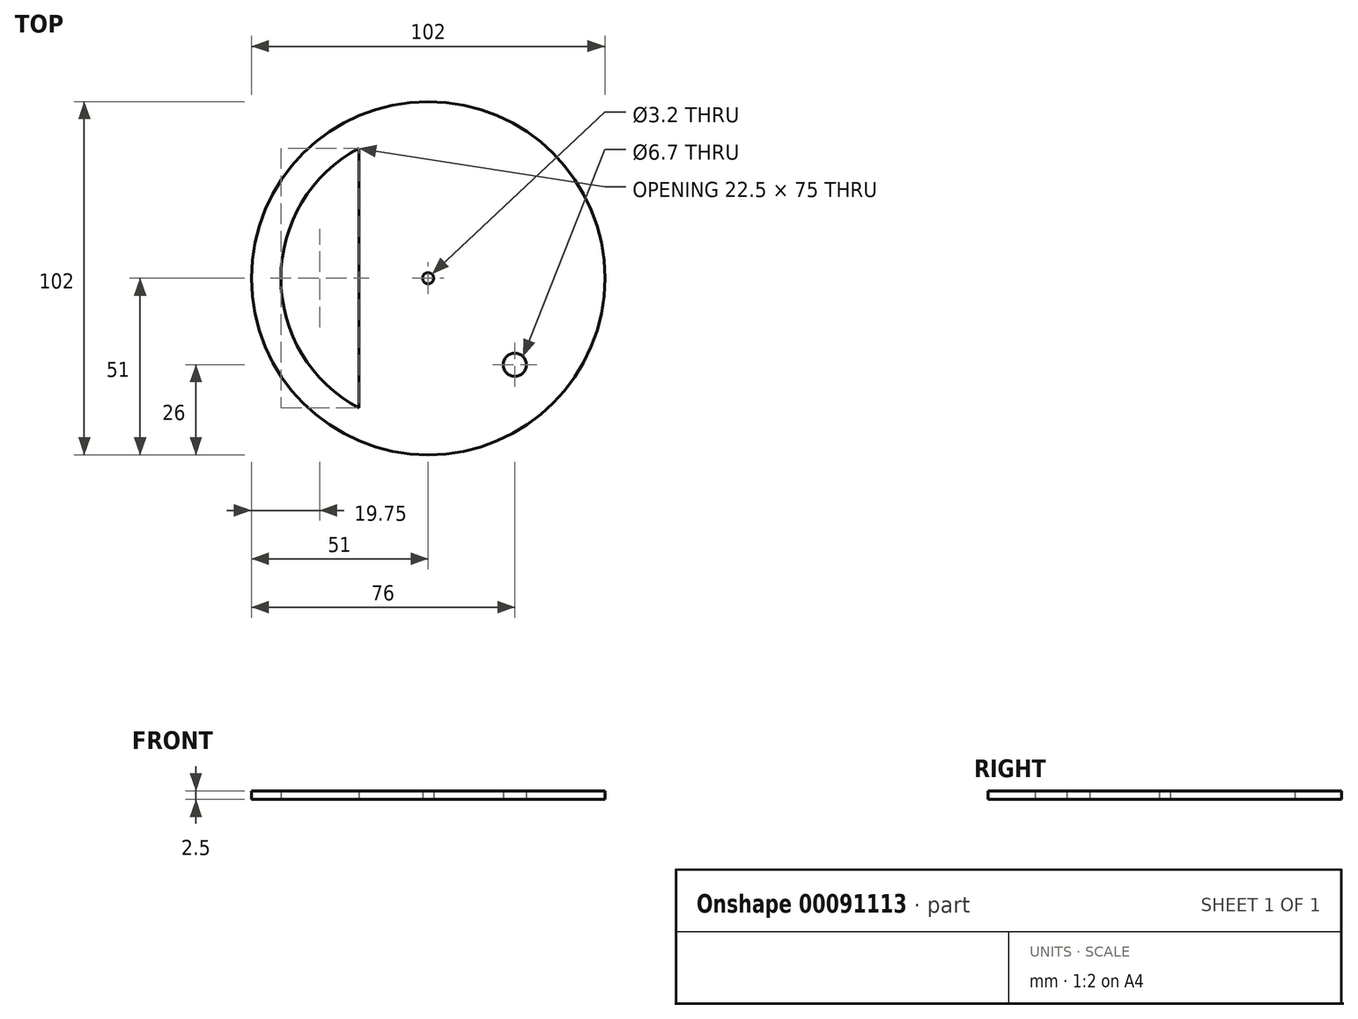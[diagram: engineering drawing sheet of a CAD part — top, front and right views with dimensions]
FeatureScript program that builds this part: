
annotation { "Feature Type Name" : "Feature", "Feature Type Description" : "" }
export const myFeature = defineFeature(function(context is Context, id is Id, definition is map)
    precondition{}
    {
        {
            var Q0;
            Q0=qCreatedBy(makeId("Top.planeOp"),FACE);
            var sketch = newSketch(context, id + "F0", { "sketchPlane" : qUnion([Q0])});
            skCircle(sketch, "E0", {"center": v(0, 0) * mm, "radius": 51 * mm});
            skCircle(sketch, "E1", {"center": v(0, 0) * mm, "radius": 42.5 * mm});
            skCircle(sketch, "E2", {"center": v(0, 0) * mm, "radius": 1.6 * mm});
            skLineSegment(sketch, "E3", {"start": v(-20, 37.5) * mm, "end": v(-20, -37.5) * mm});
            skCircle(sketch, "E4", {"center": v(25, -25) * mm, "radius": 3.35 * mm});
            skSolve(sketch);
        }
        {
            var Q0;
            Q0=makeQuery(id+"F0.imprint","IMPRINT",FACE,{"disambiguationData":[TD([[makeQuery(id+"F0.imprint","IMPRINT",EDGE,{"derivedFrom":sQuery(id+"F0.wireOp",EDGE,"E2")}),-1.0]])]});
            var Q1;
            Q1=makeQuery(id+"F0.imprint","IMPRINT",FACE,{"disambiguationData":[TD([[makeQuery(id+"F0.imprint","IMPRINT",EDGE,{"derivedFrom":sQuery(id+"F0.wireOp",EDGE,"E0")}),1.0]])]});
            extrude(context, id + "F1", {"entities" : qUnion([Q0, Q1]), "depth" : 2.5 * mm});
        }
        {
            var Q0;
            {var subQ0=sQuery(id+"F0.wireOp",EDGE,"E3");Q0=makeQuery(id+"F0.imprint","IMPRINT",FACE,{"disambiguationData":[TD([[makeQuery(id+"F0.imprint","IMPRINT",EDGE,{"derivedFrom":subQ0}),-1.0]])]});}
            extrude(context, id + "F2", {"entities" : qUnion([Q0]), "depth" : 2.5 * mm});
        }
    });
